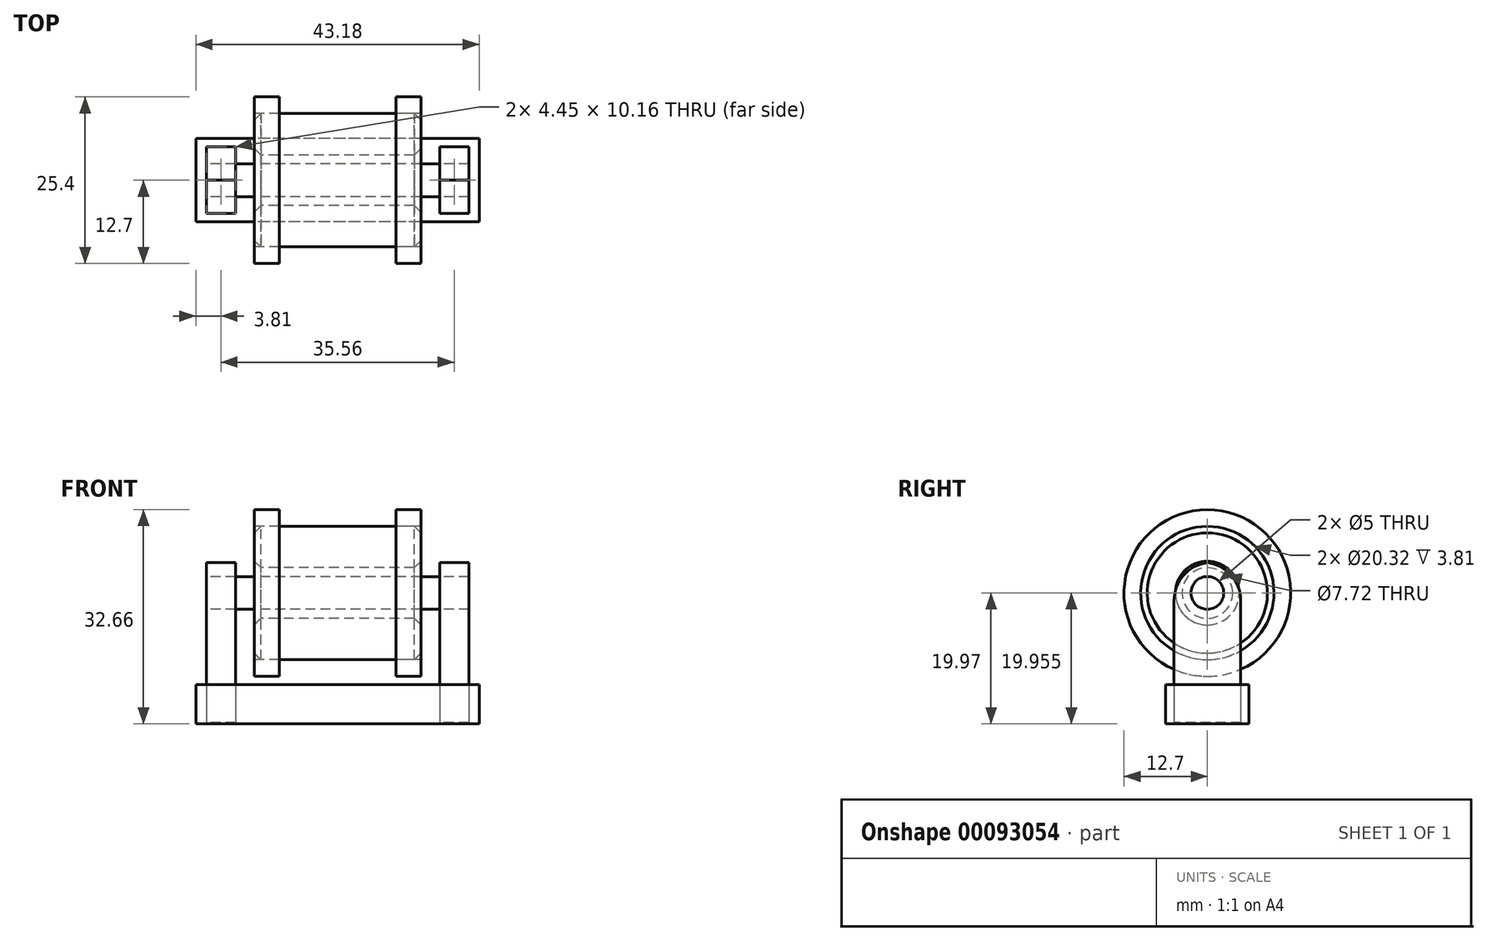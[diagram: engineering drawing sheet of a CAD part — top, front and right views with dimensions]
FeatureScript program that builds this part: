
annotation { "Feature Type Name" : "Feature", "Feature Type Description" : "" }
export const myFeature = defineFeature(function(context is Context, id is Id, definition is map)
    precondition{}
    {
        {
            var Q0;
            Q0=qCreatedBy(makeId("Top.planeOp"),FACE);
            var sketch = newSketch(context, id + "F0", { "sketchPlane" : qUnion([Q0])});
            skLineSegment(sketch, "E0.bottom", {"start": v(21.59, 6.35) * mm, "end": v(-21.59, 6.35) * mm});
            skLineSegment(sketch, "E0.top", {"start": v(21.59, -6.35) * mm, "end": v(-21.59, -6.35) * mm});
            skLineSegment(sketch, "E0.left", {"start": v(21.59, 6.35) * mm, "end": v(21.59, -6.35) * mm});
            skLineSegment(sketch, "E0.right", {"start": v(-21.59, 6.35) * mm, "end": v(-21.59, -6.35) * mm});
            skPoint(sketch, "E0.middle", {"position": v(0, 0) * mm});
            skLineSegment(sketch, "E1.bottom", {"start": v(-15.55, 5.08) * mm, "end": v(-20, 5.08) * mm});
            skLineSegment(sketch, "E1.top", {"start": v(-15.55, -5.08) * mm, "end": v(-20, -5.08) * mm});
            skLineSegment(sketch, "E1.left", {"start": v(-15.55, 5.08) * mm, "end": v(-15.55, -5.08) * mm});
            skLineSegment(sketch, "E1.right", {"start": v(-20, 5.08) * mm, "end": v(-20, -5.08) * mm});
            skPoint(sketch, "E1.middle", {"position": v(-17.78, 0) * mm});
            skLineSegment(sketch, "E2.bottom", {"start": v(20, 5.08) * mm, "end": v(15.55, 5.08) * mm});
            skLineSegment(sketch, "E2.top", {"start": v(20, -5.08) * mm, "end": v(15.55, -5.08) * mm});
            skLineSegment(sketch, "E2.left", {"start": v(20, 5.08) * mm, "end": v(20, -5.08) * mm});
            skLineSegment(sketch, "E2.right", {"start": v(15.55, 5.08) * mm, "end": v(15.55, -5.08) * mm});
            skPoint(sketch, "E2.middle", {"position": v(17.78, 0) * mm});
            skSolve(sketch);
        }
        {
            var Q0;
            Q0=makeQuery(id+"F0.imprint","IMPRINT",FACE,{"disambiguationData":[TD([[makeQuery(id+"F0.imprint","IMPRINT",EDGE,{"derivedFrom":sQuery(id+"F0.wireOp",EDGE,"E0.bottom")}),1.0]])]});
            extrude(context, id + "F1", {"entities" : qUnion([Q0]), "depth" : 6 * mm});
        }
        {
            var Q0;
            Q0=makeQuery(id+"F0.imprint","IMPRINT",FACE,{"disambiguationData":[TD([[makeQuery(id+"F0.imprint","IMPRINT",EDGE,{"derivedFrom":sQuery(id+"F0.wireOp",EDGE,"E1.bottom")}),1.0]])]});
            var Q1;
            Q1=makeQuery(id+"F0.imprint","IMPRINT",FACE,{"disambiguationData":[TD([[makeQuery(id+"F0.imprint","IMPRINT",EDGE,{"derivedFrom":sQuery(id+"F0.wireOp",EDGE,"E2.bottom")}),1.0]])]});
            var Q2;
            Q2=makeQuery(id+"F1.opExtrude","SWEPT_BODY",BODY,{"disambiguationData":[OSD([sQuery(id+"F0.wireOp",EDGE,"E0.bottom"),sQuery(id+"F0.wireOp",EDGE,"E0.top"),sQuery(id+"F0.wireOp",EDGE,"E0.left"),sQuery(id+"F0.wireOp",EDGE,"E0.right"),sQuery(id+"F0.wireOp",EDGE,"E1.bottom"),sQuery(id+"F0.wireOp",EDGE,"E1.top"),sQuery(id+"F0.wireOp",EDGE,"E1.left"),sQuery(id+"F0.wireOp",EDGE,"E1.right"),sQuery(id+"F0.wireOp",EDGE,"E2.bottom"),sQuery(id+"F0.wireOp",EDGE,"E2.top"),sQuery(id+"F0.wireOp",EDGE,"E2.left"),sQuery(id+"F0.wireOp",EDGE,"E2.right")])]});
            extrude(context, id + "F2", {"entities" : qUnion([Q0, Q1]), "depth" : 24.64 * mm, "hasSecondDirection" : true, "secondDirectionOppositeDirection" : false, "secondDirectionBoundEntityBody" : qUnion([Q2]), "secondDirectionDepth" : 0.2 * mm});
        }
        {
            var Q0;
            Q0=makeQuery(id+"F2.opExtrude","CAP_EDGE",EDGE,{"disambiguationData":[OSD([sQuery(id+"F0.wireOp",EDGE,"E2.bottom")])],"isStart":false});
            var Q1;
            Q1=makeQuery(id+"F2.opExtrude","CAP_EDGE",EDGE,{"disambiguationData":[OSD([sQuery(id+"F0.wireOp",EDGE,"E2.top")])],"isStart":false});
            var Q2;
            Q2=makeQuery(id+"F2.opExtrude","CAP_EDGE",EDGE,{"disambiguationData":[OSD([sQuery(id+"F0.wireOp",EDGE,"E1.bottom")])],"isStart":false});
            var Q3;
            Q3=makeQuery(id+"F2.opExtrude","CAP_EDGE",EDGE,{"disambiguationData":[OSD([sQuery(id+"F0.wireOp",EDGE,"E1.top")])],"isStart":false});
            fillet(context, id + "F3", {"entities" : qUnion([Q0, Q1, Q2, Q3]), "radius" : 5.84 * mm, "tangentPropagation" : true, "allowEdgeOverflow" : false});
        }
        {
            var Q0;
            Q0=makeQuery(id+"F2.opExtrude","SWEPT_FACE",FACE,{"disambiguationData":[OSD([sQuery(id+"F0.wireOp",EDGE,"E1.right")])]});
            var sketch = newSketch(context, id + "F4", { "sketchPlane" : qUnion([Q0])});
            skCircle(sketch, "E3", {"center": v(0, 19.97) * mm, "radius": 2.5 * mm});
            skSolve(sketch);
        }
        {
            var Q0;
            Q0 = qSketchRegion(id + "F4", true);
            var Q1;
            Q1=makeQuery(id+"F2.opExtrude","SWEPT_FACE",FACE,{"disambiguationData":[OSD([sQuery(id+"F0.wireOp",EDGE,"E2.left")])]});
            var Q2;
            Q2=makeQuery(id+"F2.opExtrude","SWEPT_BODY",BODY,{"disambiguationData":[OSD([sQuery(id+"F0.wireOp",EDGE,"E2.bottom"),sQuery(id+"F0.wireOp",EDGE,"E2.top"),sQuery(id+"F0.wireOp",EDGE,"E2.left"),sQuery(id+"F0.wireOp",EDGE,"E2.right")])]});
            extrude(context, id + "F5", {"entities" : qUnion([Q0]), "operationType" : NewBodyOperationType.REMOVE, "endBound" : BoundingType.UP_TO_SURFACE, "oppositeDirection" : true, "endBoundEntityFace" : qUnion([Q1]), "endBoundEntityBody" : qUnion([Q2]), "depth" : 32.45 * mm});
        }
        {
            var Q0;
            Q0 = qSketchRegion(id + "F4", true);
            var Q1;
            Q1=makeQuery(id+"F2.opExtrude","SWEPT_FACE",FACE,{"disambiguationData":[OSD([sQuery(id+"F0.wireOp",EDGE,"E2.left")])]});
            extrude(context, id + "F6", {"entities" : qUnion([Q0]), "endBound" : BoundingType.UP_TO_SURFACE, "oppositeDirection" : true, "endBoundEntityFace" : qUnion([Q1]), "depth" : 25.4 * mm});
        }
        {
            var Q0;
            Q0=qCreatedBy(makeId("Right.planeOp"),FACE);
            var sketch = newSketch(context, id + "F7", { "sketchPlane" : qUnion([Q0])});
            skCircle(sketch, "E4", {"center": v(0, 19.96) * mm, "radius": 3.86 * mm});
            skCircle(sketch, "E5", {"center": v(0, 19.96) * mm, "radius": 12.7 * mm});
            skCircle(sketch, "E6", {"center": v(0, 19.96) * mm, "radius": 10.16 * mm});
            skSolve(sketch);
        }
        {
            var Q0;
            Q0 = qSketchRegion(id + "F7", true);
            extrude(context, id + "F8", {"entities" : qUnion([Q0]), "endBound" : BoundingType.SYMMETRIC, "depth" : 25.4 * mm});
        }
        {
            var Q0;
            Q0=makeQuery(id+"F7.imprint","IMPRINT",FACE,{"disambiguationData":[TD([[makeQuery(id+"F7.imprint","IMPRINT",EDGE,{"derivedFrom":sQuery(id+"F7.wireOp",EDGE,"E4")}),-1.0]])]});
            extrude(context, id + "F9", {"entities" : qUnion([Q0]), "endBound" : BoundingType.SYMMETRIC, "depth" : 25.4 * mm});
        }
        {
            var Q0;
            Q0 = qSketchRegion(id + "F7", true);
            extrude(context, id + "F10", {"entities" : qUnion([Q0]), "operationType" : NewBodyOperationType.REMOVE, "endBound" : BoundingType.SYMMETRIC, "oppositeDirection" : true, "depth" : 17.78 * mm});
        }
        {
            var Q0;
            Q0=makeQuery(id+"F9.opExtrude","CAP_EDGE",EDGE,{"disambiguationData":[OSD([sQuery(id+"F7.wireOp",EDGE,"E4")])],"isStart":false});
            var Q1;
            Q1=makeQuery(id+"F9.opExtrude","CAP_EDGE",EDGE,{"disambiguationData":[OSD([sQuery(id+"F7.wireOp",EDGE,"E4")])],"isStart":true});
            var Q2;
            Q2=makeQuery(id+"F9.opExtrude","CAP_FACE",FACE,{"disambiguationData":[OSD([sQuery(id+"F7.wireOp",EDGE,"E4"),sQuery(id+"F7.wireOp",EDGE,"E6")])],"isStart":false});
            var Q3;
            Q3=makeQuery(id+"F9.opExtrude","SWEPT_FACE",FACE,{"disambiguationData":[OSD([sQuery(id+"F7.wireOp",EDGE,"E6")])]});
            chamfer(context, id + "F11", {"entities" : qUnion([Q0, Q1, Q2, Q3]), "width" : 1 * mm, "tangentPropagation" : true});
        }
    });
